# Revit family: Sanitary_Mirrors_Sanindusa_New-WC-Care-Adjustable-Mirror
name_source: partatom
category: Plumbing Fixtures
revit_build: Autodesk Revit 2018 (Build: 20170223_1515(x64)
units: mm (PartAtom-declared; Revit-internal decimal feet)

## family parameters
Always vertical = Yes
Cut with Voids When Loaded = No
OmniClass Number = 23.45.00.00
OmniClass Title = Sanitary, Laundry, and Cleaning Equipment
Part Type = Normal
Room Calculation Point = No
Round Connector Dimension = Use Diameter
Shared = No
Work Plane-Based = No

## types (1)
- Sanitary_Mirrors_Sanindusa_New-WC-Care-Adjustable-Mirror
    AssetType = Movable
    CodePerformance = EN 12600 classe 2B2
    Color = white
    Constituents = Fixings not included
150 mm PVC flexible hose; ABS shower bracket, with adjustable height; Fixing Kit.
    Cost = 0 $
    Description = Adjustable mirror
    Edition number = 1
    Element Type = BATHROOM MIRRORS for people with reduced mobility
    Features = Adjustable mirror.
Quick and easy installation.
Securit safety glass mirror.
Can be tilted up to 10°.
For use as a grab bar and a fixed support bar for WCs, showers or washbasins. 
Generally installed parallel to a drop-down bar in a WC or on either side of a washbasin. 
Recommended if the WC pan or shower seat is a long way from the side wall. 
In the lowered position use as a grab bar, for standing up and assisting movement. For WCs or showers. Allows side access in the raised position.
Slowed down descent. Retained in upright position.
Stainless steel  for easy maintenance and hygiene.
    Finish = Brushed
    InstallationDate = 1900-12-31T23:59:59
    Manufacturer = Sanindusa
    ManufacturerName = Sanindusa
    ManufacturerURL = www.tec.sanindusa.pt
    Material = Stainless steel
    ModelNumber = 4296913
    ModelReference = New Wccare
    Name = Adjustable mirror new wccare
    NominalHeight = 655 mm  [stored 2.14895 ft]
    NominalLength = 605 mm  [stored 1.98491 ft]
    NominalWidth = 100 mm  [stored 0.328084 ft]
    Pre-defined type (IFC) = FURNISHING ELEMENT
    Product Guid = f222559e-00e2-4372-9875-c4ef681b14cc
    Product data url = https://bimobject.com
    ProductInformation = https://www.tec.sanindusa.pt
    ProductionYear = 2017
    Size = 61x66
    Type (IFC) = IfcFurnitureType
    URL = www.tec.sanindusa.pt
    Uniclass2015Code = Pr_25_71_53_06
    Uniclass2015Title = Bathroom mirrors
    Uniclass2015Version = Products v1.6
    Version = 2
    WarrantyDescription = https://www.tec.sanindusa.pt
    WarrantyDurationParts = 5
    WarrantyDurationUnit = year
    WarrantyStartDate = 1900-12-31T23:59:59
1900-12-31T23:59:59
    Weight = 9.30 kg

note: [stored X ft] marks values corroborated as IEEE doubles in the binary element streams (Revit-internal decimal feet)

## geometry (parser evidence)
native form markers: Sweep x6
no freeform markers — native parametric forms only
